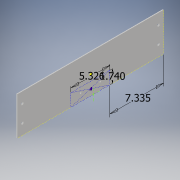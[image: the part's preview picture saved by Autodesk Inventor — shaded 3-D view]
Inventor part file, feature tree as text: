
AUTODESK INVENTOR PART (.ipt)
format: ipt  version: 2017 (Build 210142000, 142)  size: 137,216 bytes
history: native  units: in
note: dims shown in document units (in); Inventor stores cm internally (conversion verified against a paired STEP export)
features: sketch x3, hole x2, extrude x1, other x1
ambient origin geometry x8: Origin, YZ Plane, XZ Plane, XY Plane, X Axis, Y Axis, Z Axis, Center Point
bodies: Solid1 (feature_tree)
feature tree (7):
  extrude  "Extrusion1"  Depth=5.22in
  sketch  "Sketch2"  dims[d2=0.125in d3=0.0in d4=5.326in]
  hole  "Hole1"  [1 undecoded]
  hole  "Hole2"  [1 undecoded]
  sketch  "Sketch1"  dims[d0=20.0in d1=5.22in]
  sketch  "Sketch3"  dims[d5=1.74in d6=7.335in d7=1.035in d10=0.177in d11=0.75in d12=0.409in d13=0.25in d14=90.0deg d15=1.0in d16=0.8108in d17=1.332in d18=1.332in d20=0.75in d21=4.3in d22=0.46in d23=0.75in d24=4.3in d25=0.46in d26=1.0in d27=0.236in d28=1.0in d29=0.236in d30=1.0in d31=0.236in d32=1.0in d33=0.236in d34=0.169in d35=0.75in d36=0.37in d37=0.25in d38=90.0deg d39=1.0in d40=0.8108in d41=0.18in d42=0.18in]
  other  "brackets"
note: 2 required parameter values undecoded (feature->parameter linkage not recoverable at this tier; creation-order binding heuristic only, values carry confidence <= 0.55)
